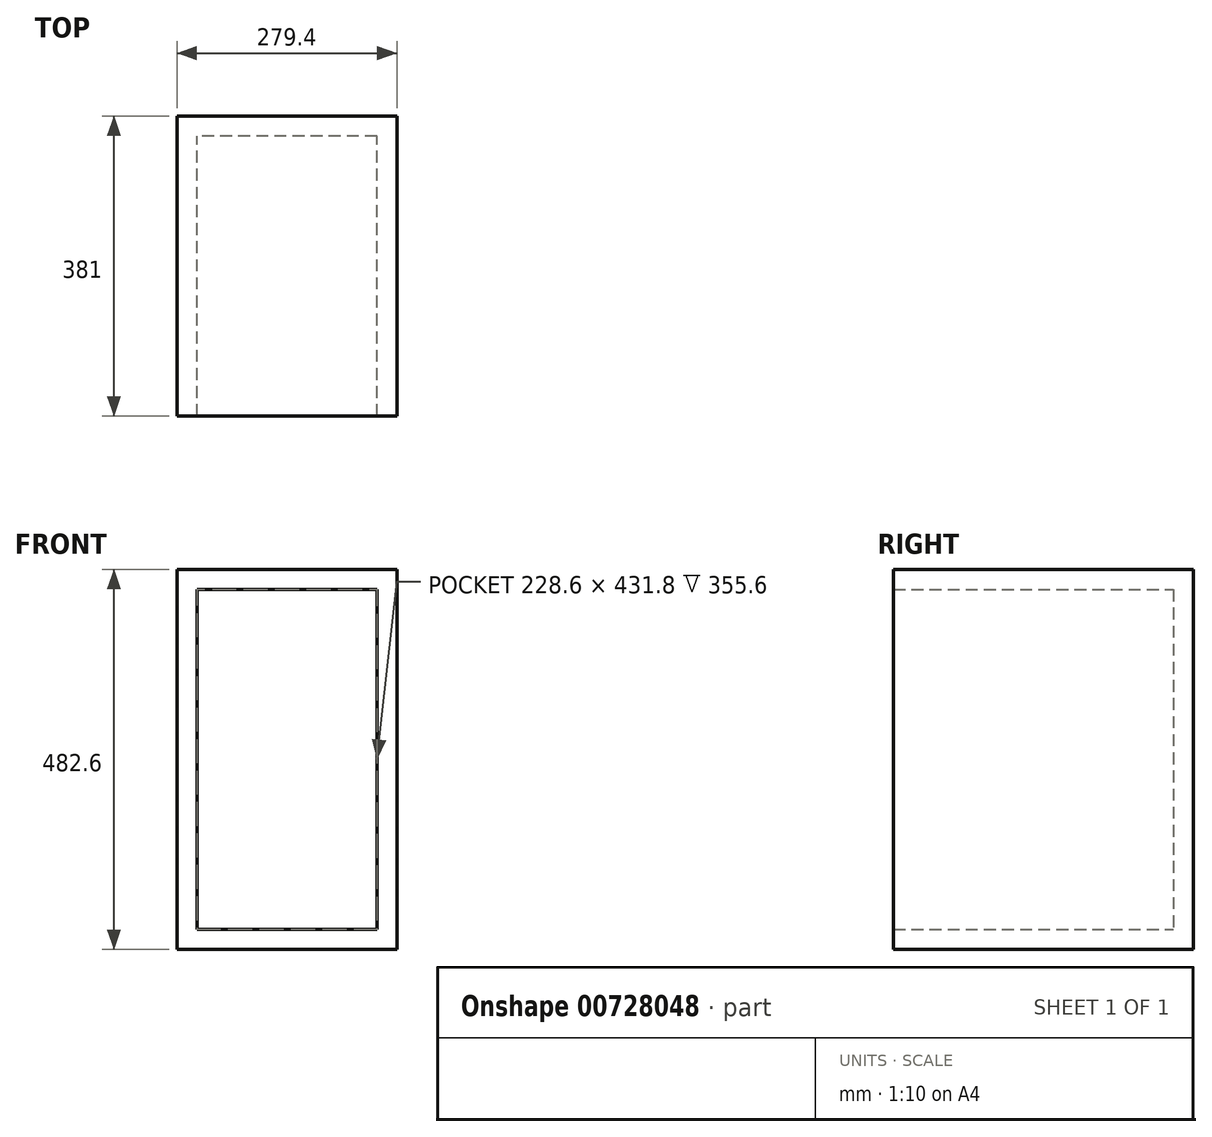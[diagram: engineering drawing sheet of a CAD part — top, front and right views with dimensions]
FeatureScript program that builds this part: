
annotation { "Feature Type Name" : "Feature", "Feature Type Description" : "" }
export const myFeature = defineFeature(function(context is Context, id is Id, definition is map)
    precondition{}
    {
        {
            var Q0;
            Q0=qCreatedBy(makeId("Front.planeOp"),FACE);
            var sketch = newSketch(context, id + "F0", { "sketchPlane" : qUnion([Q0])});
            skLineSegment(sketch, "E0.bottom", {"start": v(139.7, 241.3) * mm, "end": v(-139.7, 241.3) * mm});
            skLineSegment(sketch, "E0.top", {"start": v(139.7, -241.3) * mm, "end": v(-139.7, -241.3) * mm});
            skLineSegment(sketch, "E0.left", {"start": v(139.7, 241.3) * mm, "end": v(139.7, -241.3) * mm});
            skLineSegment(sketch, "E0.right", {"start": v(-139.7, 241.3) * mm, "end": v(-139.7, -241.3) * mm});
            skPoint(sketch, "E0.middle", {"position": v(0, 0) * mm});
            skSolve(sketch);
        }
        {
            var Q0;
            Q0=makeQuery(id+"F0.imprint","IMPRINT",FACE,{"disambiguationData":[TD([[makeQuery(id+"F0.imprint","IMPRINT",EDGE,{"derivedFrom":sQuery(id+"F0.wireOp",EDGE,"E0.bottom")}),1.0]])]});
            extrude(context, id + "F1", {"entities" : qUnion([Q0]), "depth" : 381 * mm, "offsetDistance" : 25.4 * mm});
        }
        {
            var Q0;
            Q0=makeQuery(id+"F1.opExtrude","CAP_FACE",FACE,{"disambiguationData":[OSD([sQuery(id+"F0.wireOp",EDGE,"E0.bottom"),sQuery(id+"F0.wireOp",EDGE,"E0.top"),sQuery(id+"F0.wireOp",EDGE,"E0.left"),sQuery(id+"F0.wireOp",EDGE,"E0.right")])],"isStart":false});
            var Q1;
            Q1=makeQuery(id+"F1.opExtrude","SWEPT_BODY",BODY,{"disambiguationData":[OSD([sQuery(id+"F0.wireOp",EDGE,"E0.bottom"),sQuery(id+"F0.wireOp",EDGE,"E0.top"),sQuery(id+"F0.wireOp",EDGE,"E0.left"),sQuery(id+"F0.wireOp",EDGE,"E0.right")])]});
            shell(context, id + "F2", {"entities" : qUnion([Q0]), "parts" : qUnion([Q1]), "thickness" : 25.4 * mm});
        }
    });
